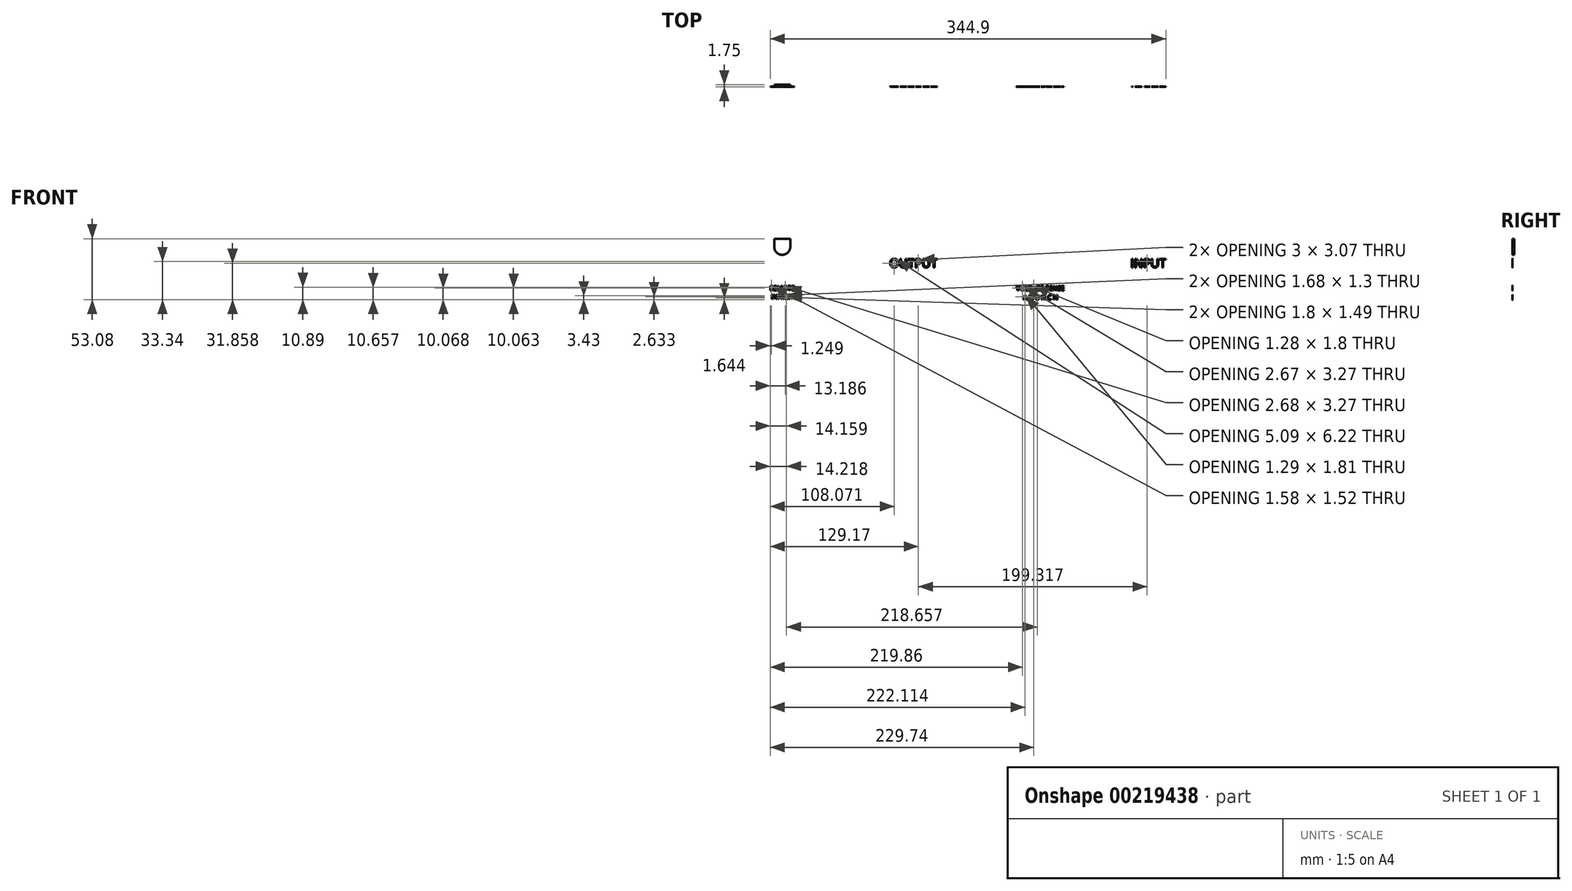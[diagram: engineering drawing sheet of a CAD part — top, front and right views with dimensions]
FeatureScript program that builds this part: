
annotation { "Feature Type Name" : "Feature", "Feature Type Description" : "" }
export const myFeature = defineFeature(function(context is Context, id is Id, definition is map)
    precondition{}
    {
        {
            var Q0;
            Q0=qCreatedBy(makeId("Front.planeOp"),FACE);
            var sketch = newSketch(context, id + "F0", { "sketchPlane" : qUnion([Q0])});
            skLineSegment(sketch, "E0.bottom", {"start": v(-241.3, 66.3) * mm, "end": v(241.3, 66.3) * mm});
            skLineSegment(sketch, "E0.top", {"start": v(-241.3, -66.3) * mm, "end": v(241.3, -66.3) * mm});
            skLineSegment(sketch, "E0.left", {"start": v(-241.3, 66.3) * mm, "end": v(-241.3, -66.3) * mm});
            skLineSegment(sketch, "E0.right", {"start": v(241.3, 66.3) * mm, "end": v(241.3, -66.3) * mm});
            skPoint(sketch, "E0.middle", {"position": v(0, 0) * mm});
            skPoint(sketch, "E1", {"position": v(-191.3, 59.3) * mm});
            skArc(sketch, "E2", {"start": v(-184.3, 59.3) * mm, "mid": v(-191.3, 52.3) * mm, "end": v(-198.3, 59.3) * mm});
            skLineSegment(sketch, "E3", {"start": v(-184.3, 59.3) * mm, "end": v(-184.3, 66.3) * mm});
            skLineSegment(sketch, "E4", {"start": v(-198.3, 59.3) * mm, "end": v(-198.3, 66.3) * mm});
            skSolve(sketch);
        }
        {
            var Q0;
            Q0=qSketchRegion(id+"F0",true);
            extrude(context, id + "F1", {"entities" : qUnion([Q0]), "oppositeDirection" : true, "depth" : 1.5 * mm, "offsetDistance" : 25.4 * mm});
        }
        {
            var Q0;
            Q0=makeQuery(id+"F0.imprint","IMPRINT",FACE,{"disambiguationData":[TD([[makeQuery(id+"F0.imprint","IMPRINT",EDGE,{"derivedFrom":sQuery(id+"F0.wireOp",EDGE,"E2")}),-1.0]])]});
            extrude(context, id + "F2", {"entities" : qUnion([Q0]), "operationType" : NewBodyOperationType.REMOVE, "oppositeDirection" : true, "depth" : 1.5 * mm, "offsetDistance" : 25.4 * mm});
        }
        {
            var Q0;
            Q0=makeQuery(id+"F1.opExtrude","CAP_FACE",FACE,{"disambiguationData":[OSD([sQuery(id+"F0.wireOp",EDGE,"E0.bottom"),sQuery(id+"F0.wireOp",EDGE,"E0.top"),sQuery(id+"F0.wireOp",EDGE,"E0.left"),sQuery(id+"F0.wireOp",EDGE,"E0.right")])],"isStart":true});
            var sketch = newSketch(context, id + "F3", { "sketchPlane" : qUnion([Q0])});
            skLineSegment(sketch, "E5.bottom", {"start": v(-230.75, 25.2) * mm, "end": v(-234.25, 25.2) * mm});
            skLineSegment(sketch, "E5.top", {"start": v(-230.75, 32) * mm, "end": v(-234.25, 32) * mm});
            skLineSegment(sketch, "E5.left", {"start": v(-230.75, 25.2) * mm, "end": v(-230.75, 32) * mm});
            skLineSegment(sketch, "E5.right", {"start": v(-234.25, 25.2) * mm, "end": v(-234.25, 32) * mm});
            skPoint(sketch, "E5.middle", {"position": v(-232.5, 28.6) * mm});
            skArc(sketch, "E6", {"start": v(-230.75, 25.2) * mm, "mid": v(-227.35, 28.6) * mm, "end": v(-230.75, 32) * mm});
            skArc(sketch, "E7", {"start": v(-234.25, 32) * mm, "mid": v(-237.65, 28.6) * mm, "end": v(-234.25, 25.2) * mm});
            skSolve(sketch);
        }
        {
            var Q0;
            Q0=makeQuery(id+"F3.imprint","IMPRINT",FACE,{"disambiguationData":[TD([[makeQuery(id+"F3.imprint","IMPRINT",EDGE,{"derivedFrom":sQuery(id+"F3.wireOp",EDGE,"E5.bottom")}),1.0]])]});
            var sketch = newSketch(context, id + "F4", { "sketchPlane" : qUnion([Q0])});
            skLineSegment(sketch, "E8.bottom", {"start": v(-230.75, -32) * mm, "end": v(-234.25, -32) * mm});
            skLineSegment(sketch, "E8.top", {"start": v(-230.75, -25.2) * mm, "end": v(-234.25, -25.2) * mm});
            skLineSegment(sketch, "E8.left", {"start": v(-230.75, -32) * mm, "end": v(-230.75, -25.2) * mm});
            skLineSegment(sketch, "E8.right", {"start": v(-234.25, -32) * mm, "end": v(-234.25, -25.2) * mm});
            skPoint(sketch, "E8.middle", {"position": v(-232.5, -28.6) * mm});
            skArc(sketch, "E9", {"start": v(-230.75, -32) * mm, "mid": v(-227.35, -28.6) * mm, "end": v(-230.75, -25.2) * mm});
            skArc(sketch, "E10", {"start": v(-234.25, -25.2) * mm, "mid": v(-237.65, -28.6) * mm, "end": v(-234.25, -32) * mm});
            skSolve(sketch);
        }
        {
            var Q0;
            Q0=makeQuery(id+"F3.imprint","IMPRINT",FACE,{"disambiguationData":[TD([[makeQuery(id+"F3.imprint","IMPRINT",EDGE,{"derivedFrom":sQuery(id+"F3.wireOp",EDGE,"E5.bottom")}),1.0]])]});
            var sketch = newSketch(context, id + "F5", { "sketchPlane" : qUnion([Q0])});
            skLineSegment(sketch, "E11.bottom", {"start": v(234.25, 32) * mm, "end": v(230.75, 32) * mm});
            skLineSegment(sketch, "E11.top", {"start": v(234.25, 25.2) * mm, "end": v(230.75, 25.2) * mm});
            skLineSegment(sketch, "E11.left", {"start": v(234.25, 32) * mm, "end": v(234.25, 25.2) * mm});
            skLineSegment(sketch, "E11.right", {"start": v(230.75, 32) * mm, "end": v(230.75, 25.2) * mm});
            skPoint(sketch, "E11.middle", {"position": v(232.5, 28.6) * mm});
            skArc(sketch, "E12", {"start": v(234.25, 25.2) * mm, "mid": v(237.65, 28.6) * mm, "end": v(234.25, 32) * mm});
            skArc(sketch, "E13", {"start": v(230.75, 32) * mm, "mid": v(227.35, 28.6) * mm, "end": v(230.75, 25.2) * mm});
            skSolve(sketch);
        }
        {
            var Q0;
            Q0=makeQuery(id+"F3.imprint","IMPRINT",FACE,{"disambiguationData":[TD([[makeQuery(id+"F3.imprint","IMPRINT",EDGE,{"derivedFrom":sQuery(id+"F3.wireOp",EDGE,"E5.bottom")}),1.0]])]});
            var sketch = newSketch(context, id + "F6", { "sketchPlane" : qUnion([Q0])});
            skLineSegment(sketch, "E14.bottom", {"start": v(234.25, -32) * mm, "end": v(230.75, -32) * mm});
            skLineSegment(sketch, "E14.top", {"start": v(234.25, -25.2) * mm, "end": v(230.75, -25.2) * mm});
            skLineSegment(sketch, "E14.left", {"start": v(234.25, -32) * mm, "end": v(234.25, -25.2) * mm});
            skLineSegment(sketch, "E14.right", {"start": v(230.75, -32) * mm, "end": v(230.75, -25.2) * mm});
            skPoint(sketch, "E14.middle", {"position": v(232.5, -28.6) * mm});
            skArc(sketch, "E15", {"start": v(230.75, -25.2) * mm, "mid": v(227.35, -28.6) * mm, "end": v(230.75, -32) * mm});
            skArc(sketch, "E16", {"start": v(234.25, -32) * mm, "mid": v(237.65, -28.6) * mm, "end": v(234.25, -25.2) * mm});
            skSolve(sketch);
        }
        {
            var Q0;
            Q0=qSketchRegion(id+"F3",true);
            var Q1;
            Q1=qSketchRegion(id+"F4",true);
            var Q2;
            Q2=qSketchRegion(id+"F5",true);
            var Q3;
            Q3=qSketchRegion(id+"F6",true);
            extrude(context, id + "F7", {"entities" : qUnion([Q0, Q1, Q2, Q3]), "operationType" : NewBodyOperationType.REMOVE, "oppositeDirection" : true, "depth" : 3 * mm});
        }
        {
            var Q0;
            Q0=makeQuery(id+"F1.opExtrude","CAP_FACE",FACE,{"disambiguationData":[OSD([sQuery(id+"F0.wireOp",EDGE,"E0.bottom"),sQuery(id+"F0.wireOp",EDGE,"E0.top"),sQuery(id+"F0.wireOp",EDGE,"E0.left"),sQuery(id+"F0.wireOp",EDGE,"E0.right")])],"isStart":true});
            var sketch = newSketch(context, id + "F8", { "sketchPlane" : qUnion([Q0])});
            skCircle(sketch, "E17", {"center": v(-76.7, 0) * mm, "radius": 32 * mm});
            skCircle(sketch, "E18", {"center": v(128.05, 0) * mm, "radius": 32 * mm});
            skLineSegment(sketch, "E19", {"start": v(54.83, 6) * mm, "end": v(12.58, 6) * mm});
            skLineSegment(sketch, "E20", {"start": v(12.58, 6) * mm, "end": v(12.58, -1.2) * mm});
            skLineSegment(sketch, "E21", {"start": v(12.58, -1.2) * mm, "end": v(16.7, -1.2) * mm});
            skLineSegment(sketch, "E22", {"start": v(16.7, -1.2) * mm, "end": v(16.7, -6.7) * mm});
            skLineSegment(sketch, "E23", {"start": v(16.7, -6.7) * mm, "end": v(50.7, -6.7) * mm});
            skLineSegment(sketch, "E24", {"start": v(50.7, -6.7) * mm, "end": v(50.7, -1.2) * mm});
            skLineSegment(sketch, "E25", {"start": v(50.7, -1.2) * mm, "end": v(54.83, -1.2) * mm});
            skLineSegment(sketch, "E26", {"start": v(54.83, -1.2) * mm, "end": v(54.83, 6) * mm});
            skCircle(sketch, "E27", {"center": v(54.04, -5) * mm, "radius": 1.6 * mm});
            skCircle(sketch, "E28", {"center": v(13.4, -5) * mm, "radius": 1.6 * mm});
            skLineSegment(sketch, "E29", {"start": v(-180.3, 6) * mm, "end": v(-202.3, 6) * mm});
            skLineSegment(sketch, "E30", {"start": v(-202.3, 6) * mm, "end": v(-202.3, -1.2) * mm});
            skLineSegment(sketch, "E31", {"start": v(-202.3, -1.2) * mm, "end": v(-198.15, -1.2) * mm});
            skLineSegment(sketch, "E32", {"start": v(-198.15, -1.2) * mm, "end": v(-198.15, -6.7) * mm});
            skLineSegment(sketch, "E33", {"start": v(-198.15, -6.7) * mm, "end": v(-184.45, -6.7) * mm});
            skLineSegment(sketch, "E34", {"start": v(-184.45, -6.7) * mm, "end": v(-184.45, -1.2) * mm});
            skLineSegment(sketch, "E35", {"start": v(-184.45, -1.2) * mm, "end": v(-180.3, -1.2) * mm});
            skLineSegment(sketch, "E36", {"start": v(-180.3, -1.2) * mm, "end": v(-180.3, 6) * mm});
            skCircle(sketch, "E37", {"center": v(-181.14, -5) * mm, "radius": 1.6 * mm});
            skCircle(sketch, "E38", {"center": v(-201.46, -5) * mm, "radius": 1.6 * mm});
            skLineSegment(sketch, "E39", {"start": v(-191.3, 10.1) * mm, "end": v(-191.3, -10.46) * mm, "construction": true});
            skSolve(sketch);
        }
        {
            var Q0;
            Q0=qSketchRegion(id+"F8",true);
            extrude(context, id + "F9", {"entities" : qUnion([Q0]), "operationType" : NewBodyOperationType.REMOVE, "oppositeDirection" : true, "depth" : 3 * mm});
        }
        {
            var Q0;
            Q0=makeQuery(id+"F1.opExtrude","CAP_FACE",FACE,{"disambiguationData":[OSD([sQuery(id+"F0.wireOp",EDGE,"E0.bottom"),sQuery(id+"F0.wireOp",EDGE,"E0.top"),sQuery(id+"F0.wireOp",EDGE,"E0.left"),sQuery(id+"F0.wireOp",EDGE,"E0.right")])],"isStart":true});
            var sketch = newSketch(context, id + "F10", { "sketchPlane" : qUnion([Q0])});
            skText(sketch, "E40", { "text": "OUTPUT", "fontName": "OpenSans-Regular.ttf"});
            skText(sketch, "E41", { "text": "INPUT", "fontName": "OpenSans-Regular.ttf"});
            skText(sketch, "E42", { "text": "VOLTAGE SENSE", "fontName": "OpenSans-Regular.ttf"});
            skText(sketch, "E43", { "text": "A N B N C N", "fontName": "OpenSans-Regular.ttf"});
            skText(sketch, "E44", { "text": "REMOTE\n INHIBIT", "fontName": "OpenSans-Regular.ttf"});
            const initialGuessF10  = {"E40": [-0.09786, 0.0413, 1, 0, 0.00762], "E41": [0.11233, 0.0413, 1, 0, 0.00762], "E42": [0.01258, 0.0213, 1, 0, 0.004], "E43": [0.01854, 0.01327, 1, 0, 0.00401], "E44": [-0.20236, 0.0213, 1, 0, 0.00401]};
            skSetInitialGuess(sketch, initialGuessF10);
            skSolve(sketch);
        }
        {
            var Q0;
            Q0=qSketchRegion(id+"F10",true);
            extrude(context, id + "F11", {"entities" : qUnion([Q0]), "operationType" : NewBodyOperationType.ADD, "depth" : 0.25 * mm, "offsetDistance" : 25.4 * mm});
        }
    });
